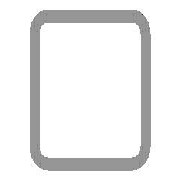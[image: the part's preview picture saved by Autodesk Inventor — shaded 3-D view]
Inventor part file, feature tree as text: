
AUTODESK INVENTOR PART (.ipt)
format: ipt  version: 2019 (Build 230136000, 136)  size: 146,944 bytes
history: native  units: mm (DEFAULTED — no unit token found)
features: other x4, plane x3, sketch x3, split x2
ambient origin geometry x8: Origin, YZ Plane, XZ Plane, XY Plane, X Axis, Y Axis, Z Axis, Center Point
bodies: Solid1 (feature_tree), Body (feature_tree)
feature tree (12):
  parser-record x1  (decoder bookkeeping rows leaked as tree rows — omitted from the tree; the rows remain in map.json)
  other  "Driven Length"
  other  "Start plane"
  other  "End plane"
  plane  "Work Plane4"
  split  "Split1"
  plane  "Work Plane5"
  split  "Split2"
  sketch  "Sketch"  dims[d7=4.0mm d9=20.0mm d11=20.0mm d12=2.0mm d13=-0.0mm d14=300.0mm d15=10.0mm d16=10.0mm d17=90.0deg d18=300.0mm]
  sketch  "Sketch3"  dims[d3=300.0mm]
  plane  "Work Plane3"
  sketch  "Sketch4"  dims[d4=0.0mm]
